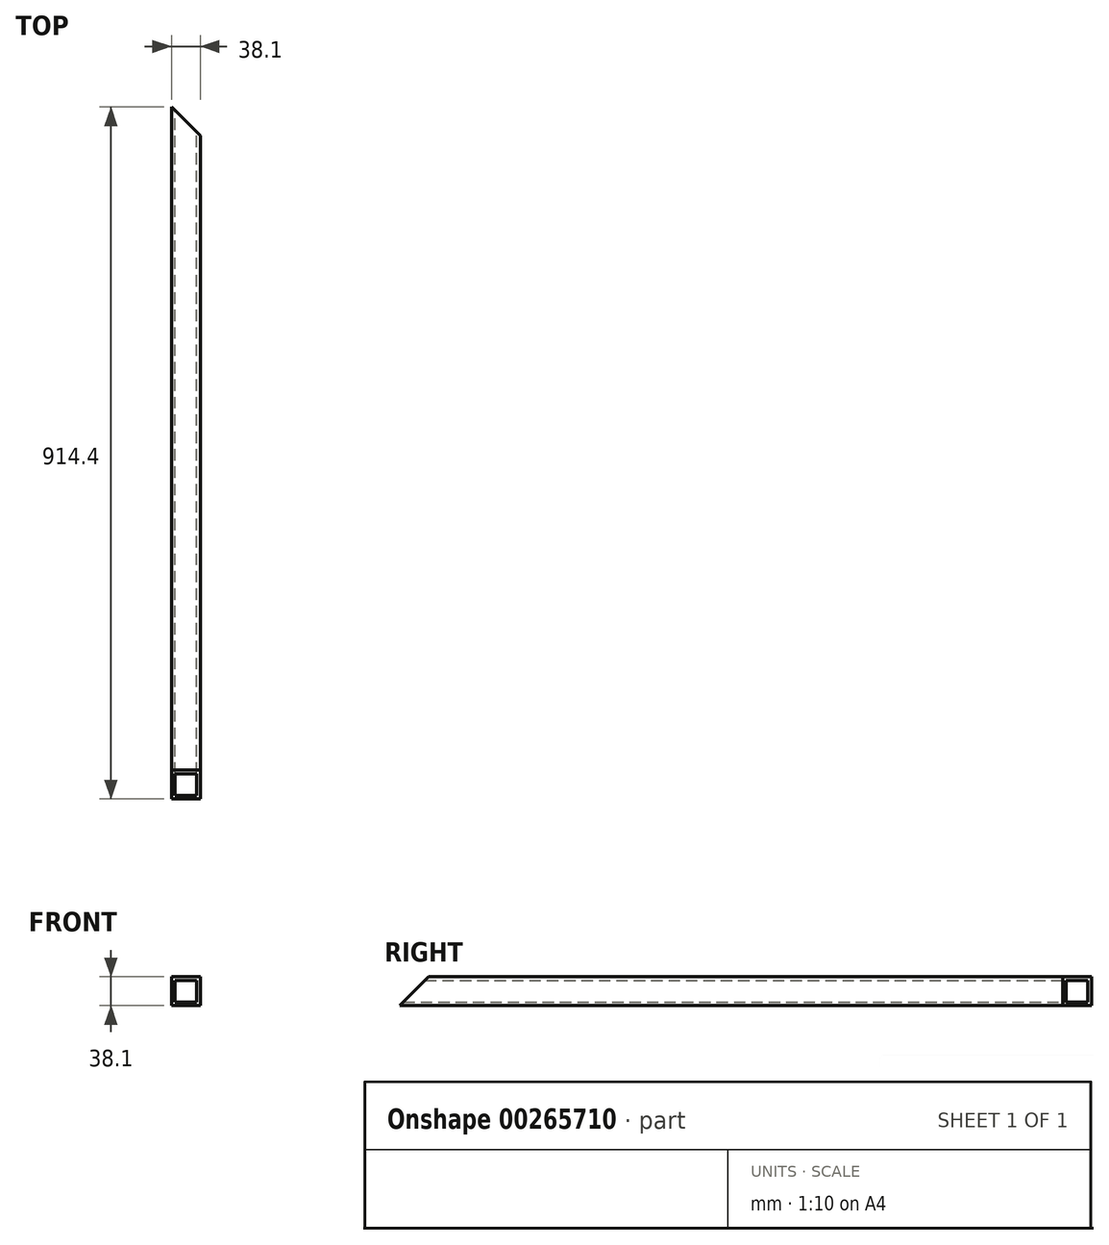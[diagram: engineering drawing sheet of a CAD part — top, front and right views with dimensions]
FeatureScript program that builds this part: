
annotation { "Feature Type Name" : "Feature", "Feature Type Description" : "" }
export const myFeature = defineFeature(function(context is Context, id is Id, definition is map)
    precondition{}
    {
        {
            var Q0;
            Q0=qCreatedBy(makeId("Front.planeOp"),FACE);
            var sketch = newSketch(context, id + "F0", { "sketchPlane" : qUnion([Q0])});
            skLineSegment(sketch, "E0.bottom", {"start": v(-19.05, 19.05) * mm, "end": v(19.05, 19.05) * mm});
            skLineSegment(sketch, "E0.top", {"start": v(-19.05, -19.05) * mm, "end": v(19.05, -19.05) * mm});
            skLineSegment(sketch, "E0.left", {"start": v(-19.05, 19.05) * mm, "end": v(-19.05, -19.05) * mm});
            skLineSegment(sketch, "E0.right", {"start": v(19.05, 19.05) * mm, "end": v(19.05, -19.05) * mm});
            skLineSegment(sketch, "E1.0", {"start": v(-14.27, 14.27) * mm, "end": v(14.27, 14.27) * mm});
            skLineSegment(sketch, "E1.1", {"start": v(-14.27, 14.27) * mm, "end": v(-14.27, -14.27) * mm});
            skLineSegment(sketch, "E1.2", {"start": v(-14.27, -14.27) * mm, "end": v(14.27, -14.27) * mm});
            skLineSegment(sketch, "E1.3", {"start": v(14.27, 14.27) * mm, "end": v(14.27, -14.27) * mm});
            skSolve(sketch);
        }
        {
            var Q0;
            Q0 = qSketchRegion(id + "F0", true);
            extrude(context, id + "F1", {"entities" : qUnion([Q0]), "depth" : 914.4 * mm});
        }
        {
            var Q0;
            Q0=makeQuery(id+"F1.opExtrude","SWEPT_FACE",FACE,{"disambiguationData":[OSD([sQuery(id+"F0.wireOp",EDGE,"E0.bottom")])]});
            var sketch = newSketch(context, id + "F2", { "sketchPlane" : qUnion([Q0])});
            skLineSegment(sketch, "E2", {"start": v(-19.05, 0) * mm, "end": v(19.05, -38.1) * mm});
            skSolve(sketch);
        }
        {
            var Q0;
            Q0=makeQuery(id+"F1.opExtrude","SWEPT_FACE",FACE,{"disambiguationData":[OSD([sQuery(id+"F0.wireOp",EDGE,"E0.left")])]});
            var sketch = newSketch(context, id + "F3", { "sketchPlane" : qUnion([Q0])});
            skLineSegment(sketch, "E3", {"start": v(914.4, -19.05) * mm, "end": v(876.3, 19.05) * mm});
            skSolve(sketch);
        }
        {
            var Q0;
            {var subQ0=sQuery(id+"F2.wireOp",EDGE,"E2");Q0=makeQuery(id+"F2.imprint","IMPRINT",FACE,{"disambiguationData":[TD([[makeQuery(id+"F2.imprint","IMPRINT",EDGE,{"derivedFrom":subQ0}),1.0]])]});}
            extrude(context, id + "F4", {"entities" : qUnion([Q0]), "operationType" : NewBodyOperationType.REMOVE, "endBound" : BoundingType.THROUGH_ALL, "oppositeDirection" : true, "depth" : 25.4 * mm});
        }
        {
            var Q0;
            {var subQ0=sQuery(id+"F3.wireOp",EDGE,"E3");Q0=makeQuery(id+"F3.imprint","IMPRINT",FACE,{"disambiguationData":[TD([[makeQuery(id+"F3.imprint","IMPRINT",EDGE,{"derivedFrom":subQ0}),-1.0]])]});}
            extrude(context, id + "F5", {"entities" : qUnion([Q0]), "operationType" : NewBodyOperationType.REMOVE, "endBound" : BoundingType.THROUGH_ALL, "oppositeDirection" : true, "depth" : 25.4 * mm});
        }
    });
